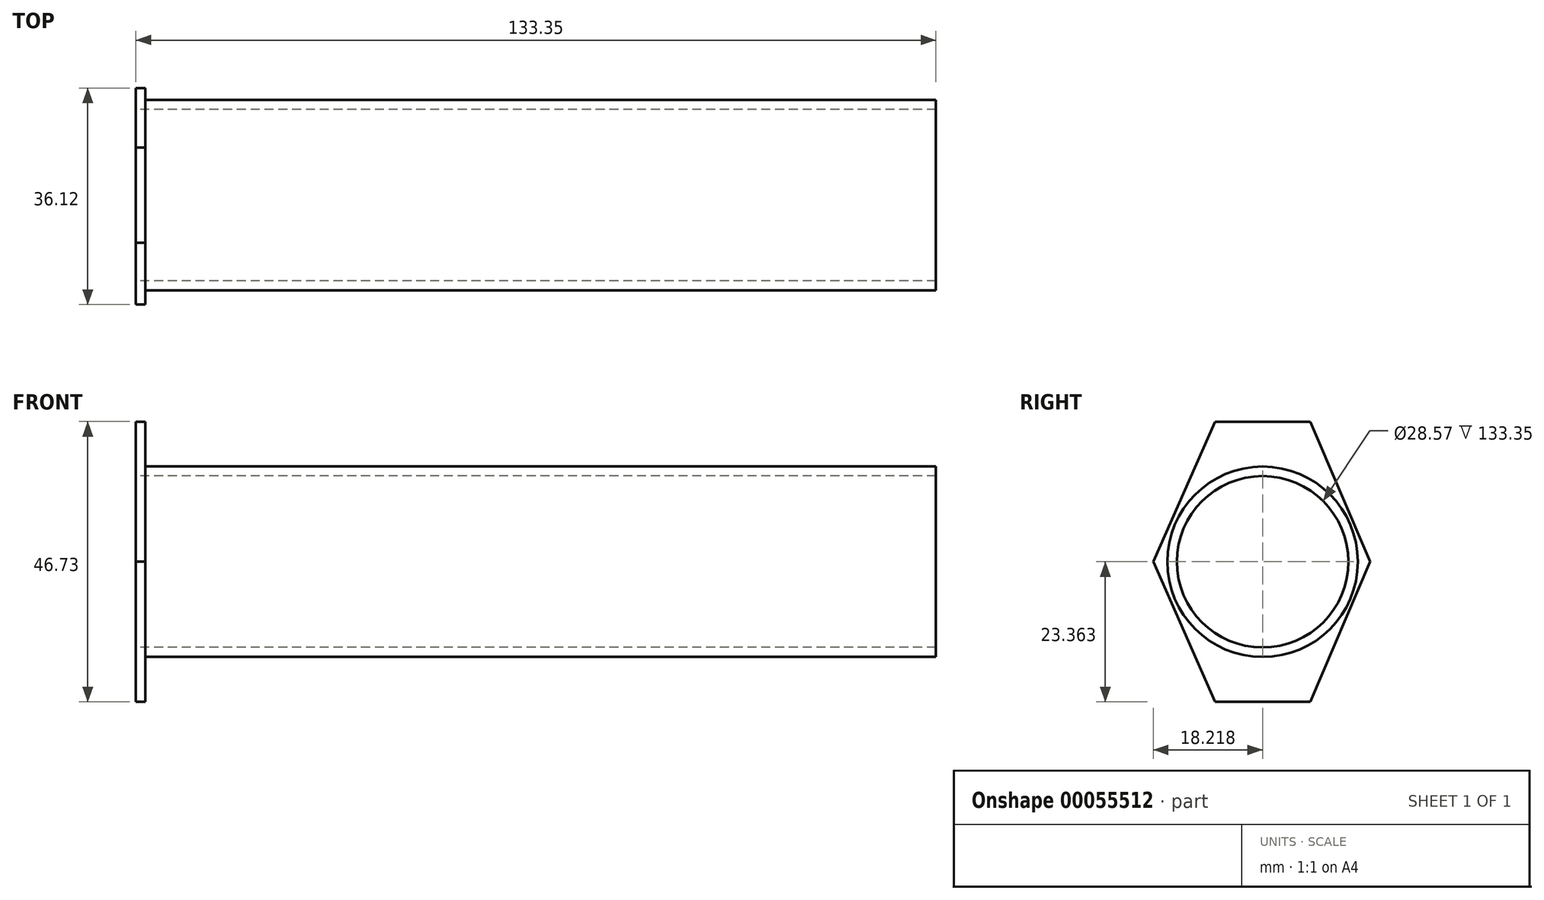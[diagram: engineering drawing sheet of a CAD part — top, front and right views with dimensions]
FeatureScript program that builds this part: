
annotation { "Feature Type Name" : "Feature", "Feature Type Description" : "" }
export const myFeature = defineFeature(function(context is Context, id is Id, definition is map)
    precondition{}
    {
        {
            var Q0;
            Q0=qCreatedBy(makeId("Right.planeOp"),FACE);
            var sketch = newSketch(context, id + "F0", { "sketchPlane" : qUnion([Q0])});
            skCircle(sketch, "E0", {"center": v(-24.27, 30.53) * mm, "radius": 15.88 * mm});
            skLineSegment(sketch, "E1", {"start": v(-24.27, 30.53) * mm, "end": v(-60.7, 30.53) * mm, "construction": true});
            skLineSegment(sketch, "E2", {"start": v(-24.27, 30.53) * mm, "end": v(13.45, 30.53) * mm, "construction": true});
            skCircle(sketch, "E3", {"center": v(-24.27, 30.53) * mm, "radius": 14.29 * mm});
            skLineSegment(sketch, "E4", {"start": v(-24.27, 30.53) * mm, "end": v(-24.27, 66.95) * mm, "construction": true});
            skLineSegment(sketch, "E5", {"start": v(-24.27, 30.53) * mm, "end": v(-24.27, -12.67) * mm, "construction": true});
            skLineSegment(sketch, "E6", {"start": v(-24.27, 7.17) * mm, "end": v(-32.2, 7.17) * mm});
            skLineSegment(sketch, "E7", {"start": v(-24.27, 7.17) * mm, "end": v(-16.33, 7.17) * mm});
            skLineSegment(sketch, "E8.MirrorCS", {"start": v(-24.27, 53.9) * mm, "end": v(-16.33, 53.9) * mm});
            skLineSegment(sketch, "E9.MirrorCS", {"start": v(-24.27, 53.9) * mm, "end": v(-32.2, 53.9) * mm});
            skLineSegment(sketch, "E10", {"start": v(-42.49, 30.53) * mm, "end": v(-32.2, 7.17) * mm});
            skLineSegment(sketch, "E11", {"start": v(-16.33, 7.17) * mm, "end": v(-6.37, 30.53) * mm});
            skLineSegment(sketch, "E12.MirrorCS", {"start": v(-42.49, 30.53) * mm, "end": v(-32.2, 53.9) * mm});
            skLineSegment(sketch, "E13.MirrorCS", {"start": v(-16.33, 53.9) * mm, "end": v(-6.37, 30.53) * mm});
            skSolve(sketch);
        }
        {
            var Q0;
            Q0 = qSketchRegion(id + "F0", true);
            extrude(context, id + "F1", {"entities" : qUnion([Q0]), "depth" : 1.59 * mm});
        }
        {
            var Q0;
            Q0=makeQuery(id+"F0.imprint","IMPRINT",FACE,{"disambiguationData":[TD([[makeQuery(id+"F0.imprint","IMPRINT",EDGE,{"derivedFrom":sQuery(id+"F0.wireOp",EDGE,"E0")}),1.0]])]});
            var Q1;
            Q1=sQuery(id+"F0.wireOp",EDGE,"E0");
            var Q2;
            Q2=sQuery(id+"F0.wireOp",EDGE,"E3");
            extrude(context, id + "F2", {"entities" : qUnion([Q0]), "operationType" : NewBodyOperationType.ADD, "surfaceEntities" : qUnion([Q1, Q2]), "depth" : 133.35 * mm});
        }
    });
